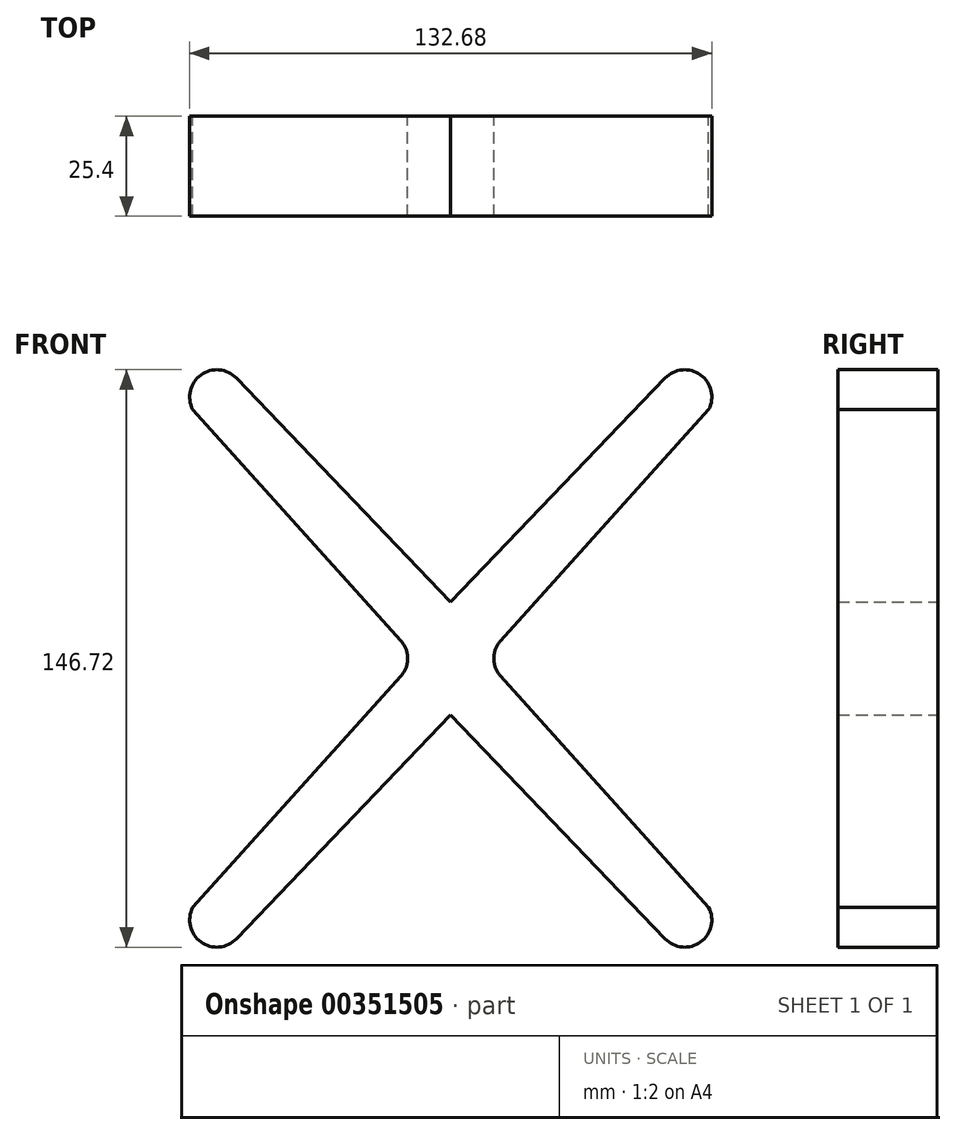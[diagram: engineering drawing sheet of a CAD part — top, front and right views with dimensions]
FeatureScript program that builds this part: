
annotation { "Feature Type Name" : "Feature", "Feature Type Description" : "" }
export const myFeature = defineFeature(function(context is Context, id is Id, definition is map)
    precondition{}
    {
        {
            var Q0;
            Q0=qCreatedBy(makeId("Front.planeOp"),FACE);
            var sketch = newSketch(context, id + "F0", { "sketchPlane" : qUnion([Q0])});
            skLineSegment(sketch, "E0", {"start": v(0, -14.35) * mm, "end": v(54.48, -71.24) * mm});
            skArc(sketch, "E1", {"start": v(54.48, -71.24) * mm, "mid": v(63.48, -72.05) * mm, "end": v(65.53, -63.25) * mm});
            skLineSegment(sketch, "E2", {"start": v(65.53, -63.25) * mm, "end": v(12.6, -4.4) * mm});
            skLineSegment(sketch, "E3.MirrorCS", {"start": v(0, -14.35) * mm, "end": v(-54.48, -71.24) * mm});
            skLineSegment(sketch, "E4.MirrorCS", {"start": v(-65.53, -63.25) * mm, "end": v(-12.6, -4.4) * mm});
            skArc(sketch, "E5.MirrorCS", {"start": v(-54.48, -71.24) * mm, "mid": v(-63.48, -72.05) * mm, "end": v(-65.53, -63.25) * mm});
            skLineSegment(sketch, "E6.MirrorCS", {"start": v(-65.53, 63.25) * mm, "end": v(-12.6, 4.4) * mm});
            skLineSegment(sketch, "E7.MirrorCS", {"start": v(0, 14.35) * mm, "end": v(-54.48, 71.24) * mm});
            skArc(sketch, "E8.MirrorCS", {"start": v(-54.48, 71.24) * mm, "mid": v(-63.48, 72.05) * mm, "end": v(-65.53, 63.25) * mm});
            skLineSegment(sketch, "E9.MirrorCS", {"start": v(65.53, 63.25) * mm, "end": v(12.6, 4.4) * mm});
            skLineSegment(sketch, "E10.MirrorCS", {"start": v(0, 14.35) * mm, "end": v(54.48, 71.24) * mm});
            skArc(sketch, "E11.MirrorCS", {"start": v(54.48, 71.24) * mm, "mid": v(63.48, 72.05) * mm, "end": v(65.53, 63.25) * mm});
            skLineSegment(sketch, "E12", {"start": v(-10.97, 0.16) * mm, "end": v(-10.97, -0.16) * mm});
            skLineSegment(sketch, "E13", {"start": v(10.97, 0.16) * mm, "end": v(10.97, -0.16) * mm});
            skPoint(sketch, "E14.visualSharp", {"position": v(-10.97, 2.6) * mm});
            skArc(sketch, "E14.filletArc", {"start": v(-10.97, 0.16) * mm, "mid": v(-11.4, 2.43) * mm, "end": v(-12.6, 4.4) * mm});
            skPoint(sketch, "E15.visualSharp", {"position": v(-10.97, -2.6) * mm});
            skArc(sketch, "E15.filletArc", {"start": v(-12.6, -4.4) * mm, "mid": v(-11.4, -2.43) * mm, "end": v(-10.97, -0.16) * mm});
            skPoint(sketch, "E16.visualSharp", {"position": v(10.97, 2.6) * mm});
            skArc(sketch, "E16.filletArc", {"start": v(12.6, 4.4) * mm, "mid": v(11.4, 2.43) * mm, "end": v(10.97, 0.16) * mm});
            skPoint(sketch, "E17.visualSharp", {"position": v(10.97, -2.6) * mm});
            skArc(sketch, "E17.filletArc", {"start": v(10.97, -0.16) * mm, "mid": v(11.4, -2.43) * mm, "end": v(12.6, -4.4) * mm});
            skSolve(sketch);
        }
        {
            var Q0;
            Q0 = qSketchRegion(id + "F0", true);
            extrude(context, id + "F1", {"entities" : qUnion([Q0]), "depth" : 25.4 * mm});
        }
    });
